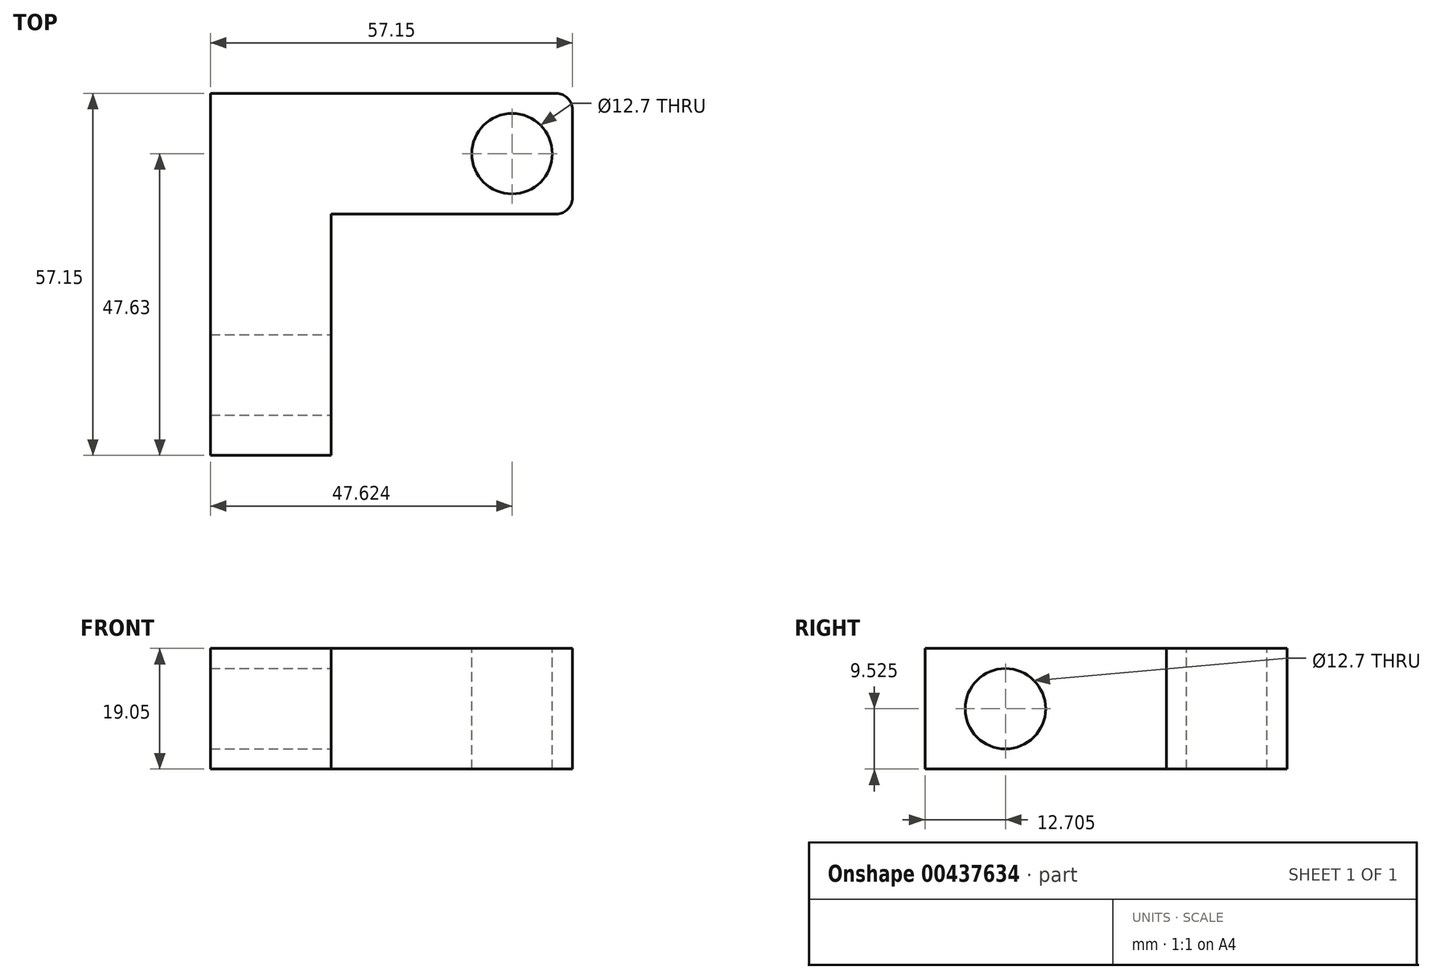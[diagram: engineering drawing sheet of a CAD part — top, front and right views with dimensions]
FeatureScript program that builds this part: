
annotation { "Feature Type Name" : "Feature", "Feature Type Description" : "" }
export const myFeature = defineFeature(function(context is Context, id is Id, definition is map)
    precondition{}
    {
        {
            var Q0;
            Q0=qCreatedBy(makeId("Top.planeOp"),FACE);
            var sketch = newSketch(context, id + "F0", { "sketchPlane" : qUnion([Q0])});
            skLineSegment(sketch, "E0", {"start": v(-12.73, -12.68) * mm, "end": v(-12.73, 44.47) * mm});
            skLineSegment(sketch, "E1", {"start": v(-12.73, 44.47) * mm, "end": v(44.42, 44.47) * mm});
            skLineSegment(sketch, "E2", {"start": v(44.42, 44.47) * mm, "end": v(44.42, 25.42) * mm});
            skLineSegment(sketch, "E3", {"start": v(44.42, 25.42) * mm, "end": v(6.32, 25.42) * mm});
            skLineSegment(sketch, "E4", {"start": v(6.32, 25.42) * mm, "end": v(6.32, -12.68) * mm});
            skLineSegment(sketch, "E5", {"start": v(6.32, -12.68) * mm, "end": v(-12.73, -12.68) * mm});
            skSolve(sketch);
        }
        {
            var Q0;
            Q0 = qSketchRegion(id + "F0", true);
            extrude(context, id + "F1", {"entities" : qUnion([Q0]), "depth" : 19.05 * mm});
        }
        {
            var Q0;
            Q0=makeQuery(id+"F1.opExtrude","CAP_FACE",FACE,{"disambiguationData":[OSD([sQuery(id+"F0.wireOp",EDGE,"E0"),sQuery(id+"F0.wireOp",EDGE,"E1"),sQuery(id+"F0.wireOp",EDGE,"E2"),sQuery(id+"F0.wireOp",EDGE,"E3"),sQuery(id+"F0.wireOp",EDGE,"E4"),sQuery(id+"F0.wireOp",EDGE,"E5")])],"isStart":false});
            var sketch = newSketch(context, id + "F2", { "sketchPlane" : qUnion([Q0])});
            skLineSegment(sketch, "E6.bottom", {"start": v(44.42, 25.42) * mm, "end": v(34.9, 25.42) * mm});
            skLineSegment(sketch, "E6.top", {"start": v(44.42, 34.95) * mm, "end": v(34.9, 34.95) * mm});
            skLineSegment(sketch, "E6.left", {"start": v(44.42, 25.42) * mm, "end": v(44.42, 34.95) * mm});
            skLineSegment(sketch, "E6.right", {"start": v(34.9, 25.42) * mm, "end": v(34.9, 34.95) * mm});
            skSolve(sketch);
        }
        {
            var Q0;
            Q0=sQuery(id+"F2.wireOp",VERTEX,"E6.top.end");
            var Q1;
            Q1=makeQuery(id+"F1.opExtrude","SWEPT_BODY",BODY,{"disambiguationData":[OSD([sQuery(id+"F0.wireOp",EDGE,"E0"),sQuery(id+"F0.wireOp",EDGE,"E1"),sQuery(id+"F0.wireOp",EDGE,"E2"),sQuery(id+"F0.wireOp",EDGE,"E3"),sQuery(id+"F0.wireOp",EDGE,"E4"),sQuery(id+"F0.wireOp",EDGE,"E5")])]});
            hole(context, id + "F3", {"style" : HoleStyle.SIMPLE, "endStyle" : HoleEndStyle.THROUGH, "holeDiameter" : 12.7 * mm, "isTappedThrough" : true, "tappedDepth" : 12.7 * mm, "tapClearance" : 3, "startFromSketch" : true, "locations" : qUnion([Q0]), "scope" : qUnion([Q1])});
        }
        {
            var Q0;
            Q0=makeQuery(id+"F1.opExtrude","SWEPT_EDGE",EDGE,{"disambiguationData":[OSD([sQuery(id+"F0.wireOp",EDGE,"E2"),sQuery(id+"F0.wireOp",EDGE,"E3")])]});
            var Q1;
            Q1=makeQuery(id+"F1.opExtrude","SWEPT_EDGE",EDGE,{"disambiguationData":[OSD([sQuery(id+"F0.wireOp",EDGE,"E1"),sQuery(id+"F0.wireOp",EDGE,"E2")])]});
            fillet(context, id + "F4", {"entities" : qUnion([Q0, Q1]), "radius" : 2.54 * mm, "tangentPropagation" : true, "allowEdgeOverflow" : false});
        }
        {
            var Q0;
            Q0=makeQuery(id+"F1.opExtrude","SWEPT_FACE",FACE,{"disambiguationData":[OSD([sQuery(id+"F0.wireOp",EDGE,"E4")])]});
            var sketch = newSketch(context, id + "F5", { "sketchPlane" : qUnion([Q0])});
            skLineSegment(sketch, "E7.bottom", {"start": v(-12.68, 0) * mm, "end": v(0.02, 0) * mm});
            skLineSegment(sketch, "E7.top", {"start": v(-12.68, 9.53) * mm, "end": v(0.02, 9.53) * mm});
            skLineSegment(sketch, "E7.left", {"start": v(-12.68, 0) * mm, "end": v(-12.68, 9.53) * mm});
            skLineSegment(sketch, "E7.right", {"start": v(0.02, 0) * mm, "end": v(0.02, 9.53) * mm});
            skSolve(sketch);
        }
        {
            var Q0;
            Q0=sQuery(id+"F5.wireOp",VERTEX,"vXfCH1Dw-3xEQ-0aDy-ou59-6afDzLQGSLXG.right.end");
            var Q1;
            Q1=sQuery(id+"F5.wireOp",VERTEX,"E7.right.end");
            var Q2;
            Q2=makeQuery(id+"F1.opExtrude","SWEPT_BODY",BODY,{"disambiguationData":[OSD([sQuery(id+"F0.wireOp",EDGE,"E0"),sQuery(id+"F0.wireOp",EDGE,"E1"),sQuery(id+"F0.wireOp",EDGE,"E2"),sQuery(id+"F0.wireOp",EDGE,"E3"),sQuery(id+"F0.wireOp",EDGE,"E4"),sQuery(id+"F0.wireOp",EDGE,"E5")])]});
            hole(context, id + "F6", {"style" : HoleStyle.SIMPLE, "endStyle" : HoleEndStyle.THROUGH, "holeDiameter" : 12.7 * mm, "isTappedThrough" : true, "tappedDepth" : 12.7 * mm, "tapClearance" : 3, "startFromSketch" : true, "locations" : qUnion([Q0, Q1]), "scope" : qUnion([Q2])});
        }
    });
